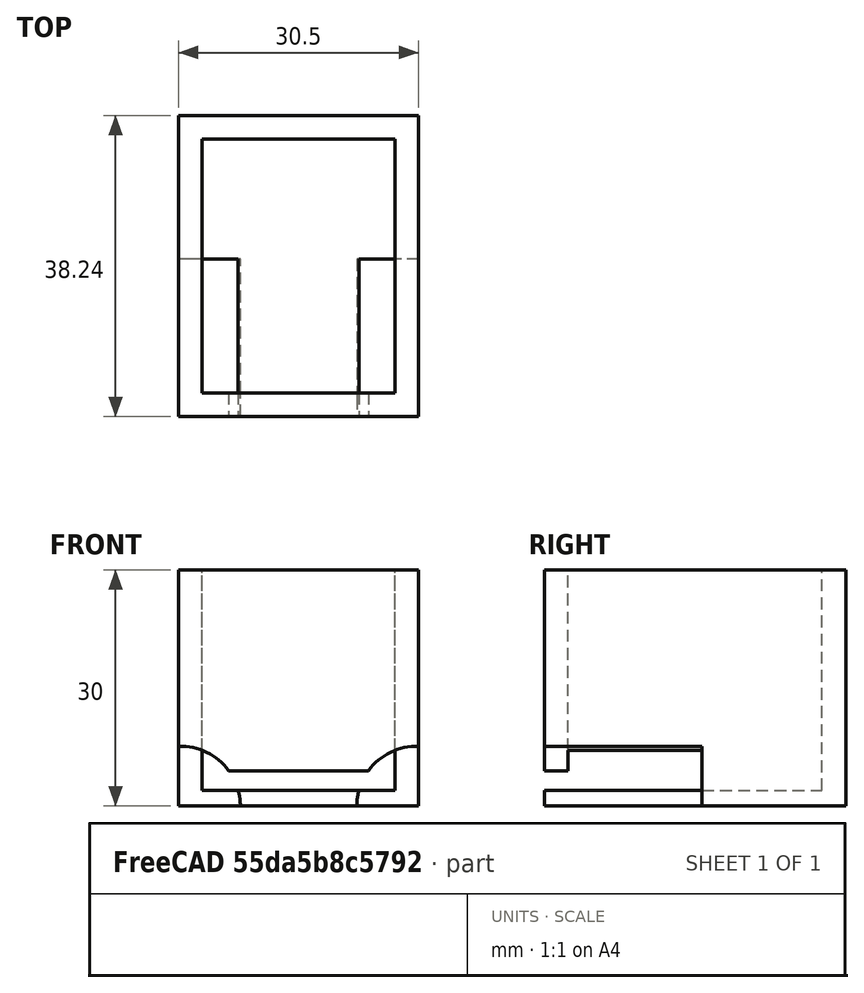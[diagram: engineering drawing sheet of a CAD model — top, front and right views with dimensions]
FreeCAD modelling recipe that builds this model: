
FCSTD DOCUMENT  (FreeCAD 0.19R)
Label: SDmagazine
License: All rights reserved
LicenseURL: http://en.wikipedia.org/wiki/All_rights_reserved
objects: Sketcher::SketchObject×4, PartDesign::Pad×2, PartDesign::Pocket×2, PartDesign::Body×1, Mesh::Feature×1
note: 13 computed .brp shape members not serialized (recipe doc carries the construction recipe); baked Part::Feature solids carry a one-line shape summary decoded from their .brp

FEATURE [Sketcher::SketchObject] Sketch
  FullyConstrained = true
  MapMode = 5
  Support = -> [XY_Plane]
  sketch-geometry (8):
    g0: LineSegment StartX=-12.25 StartY=16.125 StartZ=0 EndX=12.25 EndY=16.125 EndZ=0
    g1: LineSegment StartX=12.25 StartY=16.125 StartZ=0 EndX=12.25 EndY=-16.125 EndZ=0
    g2: LineSegment StartX=12.25 StartY=-16.125 StartZ=0 EndX=-12.25 EndY=-16.125 EndZ=0
    g3: LineSegment StartX=-12.25 StartY=-16.125 StartZ=0 EndX=-12.25 EndY=16.125 EndZ=0
    g4: LineSegment StartX=-15.25 StartY=19.125 StartZ=0 EndX=15.25 EndY=19.125 EndZ=0
    g5: LineSegment StartX=15.25 StartY=19.125 StartZ=0 EndX=15.25 EndY=-19.125 EndZ=0
    g6: LineSegment StartX=15.25 StartY=-19.125 StartZ=0 EndX=-15.25 EndY=-19.125 EndZ=0
    g7: LineSegment StartX=-15.25 StartY=-19.125 StartZ=0 EndX=-15.25 EndY=19.125 EndZ=0
  constraints (22):
    c: Coincident(g0,g1)
    c: Coincident(g1,g2)
    c: Coincident(g2,g3)
    c: Coincident(g3,g0)
    c: Horizontal(g0)
    c: Horizontal(g2)
    c: Vertical(g1)
    c: Vertical(g3)
    c: Symmetric(g1,g0,g-1)
    c: Distance(g0) = 24.5
    c: Distance(g1) = 32.25
    c: Coincident(g4,g5)
    c: Coincident(g5,g6)
    c: Coincident(g6,g7)
    c: Coincident(g7,g4)
    c: Horizontal(g4)
    c: Horizontal(g6)
    c: Vertical(g5)
    c: Vertical(g7)
    c: Symmetric(g5,g4,g-1)
    c: Distance(g0,g4) = 3
    c: Distance(g0,g5) = 3
FEATURE [PartDesign::Pad] Pad
  Direction = (1,1,1)
  Length = 30
  Length2 = 100
  Profile = -> Sketch
  Type = 0
FEATURE [Sketcher::SketchObject] Sketch001
  FullyConstrained = false
  MapMode = 5
  Placement = pos=(0,0,0) rot=(1,0,0;3.14159rad)
  Support = -> [Pad]
  sketch-geometry (4):
    g0: LineSegment StartX=-13.0641 StartY=16.7152 StartZ=0 EndX=13.0641 EndY=16.7152 EndZ=0
    g1: LineSegment StartX=13.0641 StartY=16.7152 StartZ=0 EndX=13.0641 EndY=-16.7152 EndZ=0
    g2: LineSegment StartX=13.0641 StartY=-16.7152 StartZ=0 EndX=-13.0641 EndY=-16.7152 EndZ=0
    g3: LineSegment StartX=-13.0641 StartY=-16.7152 StartZ=0 EndX=-13.0641 EndY=16.7152 EndZ=0
  constraints (9):
    c: Coincident(g0,g1)
    c: Coincident(g1,g2)
    c: Coincident(g2,g3)
    c: Coincident(g3,g0)
    c: Horizontal(g0)
    c: Horizontal(g2)
    c: Vertical(g1)
    c: Vertical(g3)
    c: Symmetric(g1,g0,g-1)
FEATURE [PartDesign::Pad] Pad001
  BaseFeature = -> Pad
  Direction = (1,1,1)
  Length = 2
  Length2 = 100
  Profile = -> Sketch001
  Reversed = true
  Type = 0
FEATURE [Sketcher::SketchObject] Sketch002
  FullyConstrained = true
  MapMode = 5
  Placement = pos=(0,-19.125,0) rot=(1,0,0;1.5708rad)
  Support = -> [Pad001]
  sketch-geometry (2):
    g0: Circle CenterX=15 CenterY=0 CenterZ=0 NormalX=0 NormalY=0 NormalZ=1 AngleXU=0 Radius=7.6
    g1: Circle CenterX=-15 CenterY=0 CenterZ=0 NormalX=0 NormalY=0 NormalZ=1 AngleXU=0 Radius=7.6
  constraints (5):
    c: Symmetric(g1,g0,g-2)
    c: Diameter(g1) = 15.2
    c: Equal(g1,g0)
    c: PointOnObject(g0,g-1)
    c: DistanceX(g0) = 15
FEATURE [PartDesign::Pocket] Pocket
  BaseFeature = -> Pad001
  Length = 20
  Length2 = 100
  Profile = -> Sketch002
  Type = 0
FEATURE [Sketcher::SketchObject] Sketch003
  FullyConstrained = false
  MapMode = 5
  Placement = pos=(0,-19.125,0) rot=(1,0,0;1.5708rad)
  Support = -> [Pocket]
  sketch-geometry (4):
    g0: LineSegment StartX=-9.71651 StartY=4.5 StartZ=0 EndX=9.94452 EndY=4.5 EndZ=0
    g1: LineSegment StartX=9.94452 StartY=4.5 StartZ=0 EndX=9.94452 EndY=2 EndZ=0
    g2: LineSegment StartX=9.94452 StartY=2 StartZ=0 EndX=-9.71651 EndY=2 EndZ=0
    g3: LineSegment StartX=-9.71651 StartY=2 StartZ=0 EndX=-9.71651 EndY=4.5 EndZ=0
  constraints (10):
    c: Coincident(g0,g1)
    c: Coincident(g1,g2)
    c: Coincident(g2,g3)
    c: Coincident(g3,g0)
    c: Horizontal(g0)
    c: Horizontal(g2)
    c: Vertical(g1)
    c: Vertical(g3)
    c: Distance(g1) = 2.5
    c: DistanceY(g1) = 2
FEATURE [PartDesign::Pocket] Pocket001
  BaseFeature = -> Pocket
  Length = 5
  Length2 = 100
  Profile = -> Sketch003
  Type = 0
FEATURE [PartDesign::Body] Body
  Group = -> [Sketch,Pad,Sketch001,Pad001,Sketch002,Pocket,Sketch003,Pocket001]
  Origin = -> Origin
  Tip = -> Pocket001
FEATURE [Mesh::Feature] Mesh  label="Pocket001 (Meshed)"
